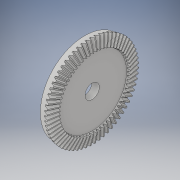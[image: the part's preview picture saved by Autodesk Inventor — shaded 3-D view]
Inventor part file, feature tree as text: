
AUTODESK INVENTOR PART (.ipt)
format: ipt  version: 2019.3 (Build 233278000, 278)  size: 616,960 bytes
history: native  units: in
note: dims shown in document units (in); Inventor stores cm internally (conversion verified against a paired STEP export)
features: extrude x1, sketch x1, other x1
ambient origin geometry x8: Origin, YZ Plane, XZ Plane, XY Plane, X Axis, Y Axis, Z Axis, Center Point
bodies: Solid1 (feature_tree)
feature tree (3):
  extrude  "Extrusion1"  [1 undecoded]
  sketch  "Sketch1"  dims[d0=1.0in d1=0.0in]
  parser-record x1  (decoder bookkeeping rows leaked as tree rows — omitted from the tree; the rows remain in map.json)
note: 1 required parameter value undecoded (feature->parameter linkage not recoverable at this tier; creation-order binding heuristic only, values carry confidence <= 0.55)
